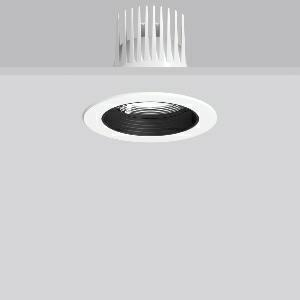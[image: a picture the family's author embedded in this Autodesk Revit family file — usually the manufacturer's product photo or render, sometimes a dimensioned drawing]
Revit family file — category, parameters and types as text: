
# Revit family: heledon_maxi_e_901768_002_2_898f
name_source: partatom
category: Lighting Fixtures
units: mm (PartAtom-declared; Revit-internal decimal feet)

## family parameters
Cut with Voids When Loaded = No
Host = Face
Light Source = No
Part Type = Normal
Room Calculation Point = No
Round Connector Dimension = Use Diameter
Shared = No

## types (1)
- HELEDON maxi E (1 x LED Modul 927, 3350 lm, 2700)
    Apparent Load = 35 VA
    Approval mark = CE
    CIE Flux Codes = 96 100 100 100 100
    Color Rendering = 92
    Color Temperature = 2700
    Default Elevation = 1800 mm
    Description = Series: HELEDON maxi
Round recessed downlight. Housing: die-cast aluminium, powder-coated. Black plastic ring and recessed LED to prevent glare from the side. Optical assembly with lens made of plastic (polycarbonate) for the best homogeneous light distribution - can be changed without tools. Best colour rendering index Ra>90. Suitable for Recessed ceiling mounting. Installation without tools thanks to spring fastening system. Including separate LED converter with connecting cable 600 mm.High quality converter without flickering and stroboscopic effect. Through-wiring box (5 pole) available as accessory. The following accessories can be mounted without use of tools: interchangeable lenses, decorative glasses, honeycomb louvre, clear and frosted diffusers, white interchangeable plastic ring. 
Colour: traffic white, matt (RAL 9016)
Diameter: 162 mm
Height: 3 mm
Cut-out diameter: 152 mm
Recess height: 200 mm
Luminaire: recess height: 135 mm
Lamp: LED
Socket: without socket
Colour temperature: 2700K
Colour rendering index (CRI): 92
System power: 35 W
Rated luminous flux: 3350 lm
Luminous efficiency: 96 lm/W
Control gear: Regulated power supply
Protection class: II
Type of protection: IP 20
    Height = 0 mm  [stored 0 ft]
    Lamp = 1 x LED Modul 927
    Lamp Light Flux = 3350 lm
    Lamp count = 1
    Length = 162 mm
    Lifetime = 50000 h
    Luminous efficacy = 96 lm/W
    Manufacturer = RZB
    ModVariant = No
    Model = 901768.002.2
    Mounting Place = Ceiling
    Mounting Type = Recessed
    Number of Poles = 1
    OnlyDefault = Yes
    Power Factor = 1
    Product Name = HELEDON maxi E
    Product group = Recessed downlights
    ProductGroupID = 402
    Protection Class = Protection class II
    Protection Degree = IP 20
    RLX_Detail_Level = 1
    RLX_Emergency_Light_Flux = 0 lm
    RLX_Emergency_Type = 0
    RLX_Emergency_Type_DB = No
    RlxData = <blob elided: 118885 chars, md5=0ace515a>
    Socket = socket
    Standby Power = 0 W
    System Light Flux = 3350 lm
    System Power = 35 W
    Type Comments = Product without accessories
    Type Image = 901663.002.jpg
    URL = http://relux.com
    VarID = ---
    Voltage = 230 V
    Voltage Range = 220-240 V
    Weight = 0.00 kg
    Width = 0 mm  [stored 0 ft]

note: [stored X ft] marks values corroborated as IEEE doubles in the binary element streams (Revit-internal decimal feet)

## geometry (parser evidence)
native form markers: Blend x4, Sweep x11
no freeform markers — native parametric forms only
